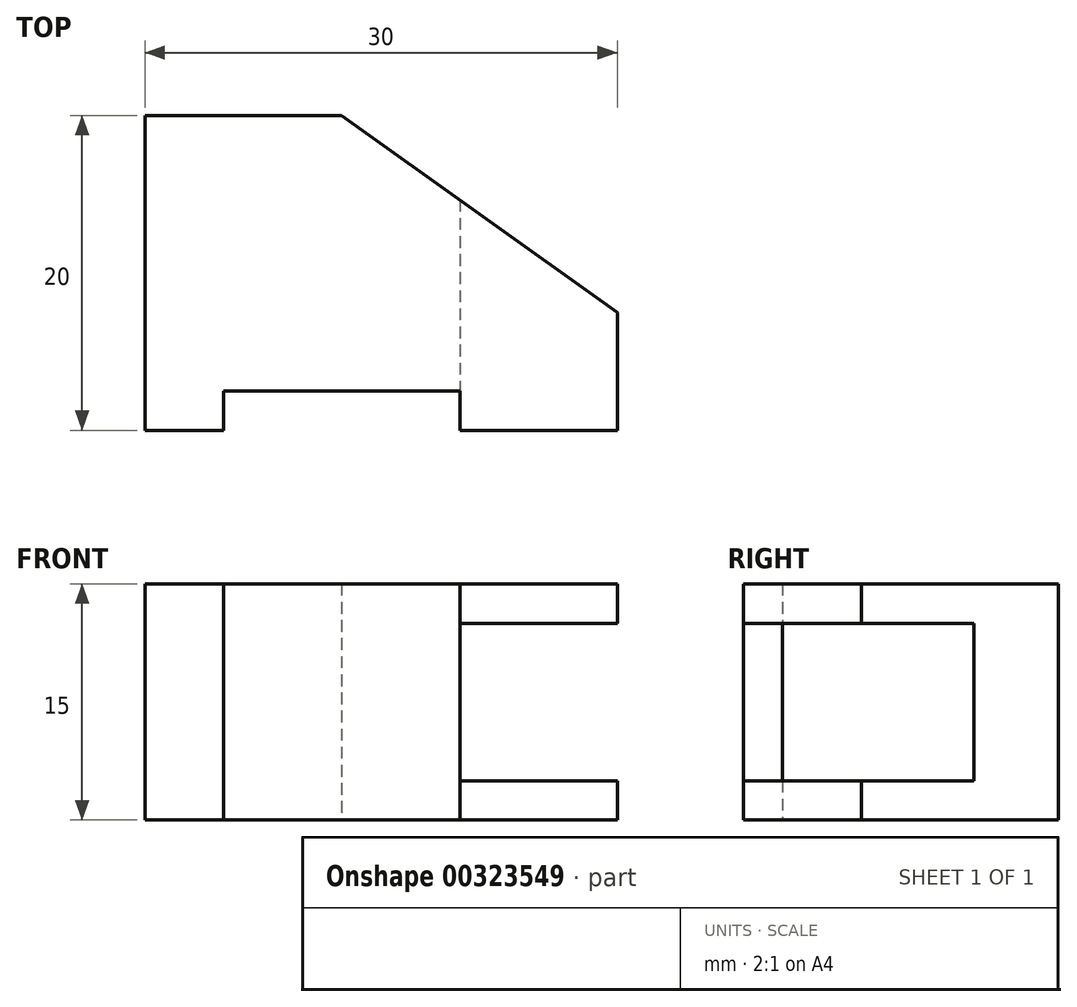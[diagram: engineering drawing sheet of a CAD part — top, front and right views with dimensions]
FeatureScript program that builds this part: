
annotation { "Feature Type Name" : "Feature", "Feature Type Description" : "" }
export const myFeature = defineFeature(function(context is Context, id is Id, definition is map)
    precondition{}
    {
        {
            var Q0;
            Q0=qCreatedBy(makeId("Top.planeOp"),FACE);
            var sketch = newSketch(context, id + "F0", { "sketchPlane" : qUnion([Q0])});
            skLineSegment(sketch, "E0", {"start": v(0, 0) * mm, "end": v(0, 20) * mm});
            skLineSegment(sketch, "E1", {"start": v(0, 20) * mm, "end": v(12.5, 20) * mm});
            skLineSegment(sketch, "E2", {"start": v(12.5, 20) * mm, "end": v(30, 7.5) * mm});
            skLineSegment(sketch, "E3", {"start": v(30, 7.5) * mm, "end": v(30, 0) * mm});
            skLineSegment(sketch, "E4", {"start": v(30, 0) * mm, "end": v(20, 0) * mm});
            skLineSegment(sketch, "E5", {"start": v(20, 0) * mm, "end": v(20, 2.5) * mm});
            skLineSegment(sketch, "E6", {"start": v(20, 2.5) * mm, "end": v(5, 2.5) * mm});
            skLineSegment(sketch, "E7", {"start": v(5, 2.5) * mm, "end": v(5, 0) * mm});
            skLineSegment(sketch, "E8", {"start": v(5, 0) * mm, "end": v(0, 0) * mm});
            skSolve(sketch);
        }
        {
            var Q0;
            Q0 = qSketchRegion(id + "F0", true);
            extrude(context, id + "F1", {"entities" : qUnion([Q0]), "depth" : 2.5 * mm});
        }
        {
            var Q0;
            Q0=makeQuery(id+"F1.opExtrude","CAP_FACE",FACE,{"disambiguationData":[OSD([sQuery(id+"F0.wireOp",EDGE,"E0"),sQuery(id+"F0.wireOp",EDGE,"E1"),sQuery(id+"F0.wireOp",EDGE,"E2"),sQuery(id+"F0.wireOp",EDGE,"E3"),sQuery(id+"F0.wireOp",EDGE,"E4"),sQuery(id+"F0.wireOp",EDGE,"E5"),sQuery(id+"F0.wireOp",EDGE,"E6"),sQuery(id+"F0.wireOp",EDGE,"E7"),sQuery(id+"F0.wireOp",EDGE,"E8")])],"isStart":false});
            var sketch = newSketch(context, id + "F2", { "sketchPlane" : qUnion([Q0])});
            skLineSegment(sketch, "E9", {"start": v(0, 0) * mm, "end": v(0, 20) * mm});
            skLineSegment(sketch, "E10", {"start": v(0, 20) * mm, "end": v(12.5, 20) * mm});
            skLineSegment(sketch, "E11", {"start": v(12.5, 20) * mm, "end": v(20, 14.64) * mm});
            skLineSegment(sketch, "E12", {"start": v(20, 14.64) * mm, "end": v(20, 0) * mm});
            skLineSegment(sketch, "E13", {"start": v(20, 0) * mm, "end": v(20, 2.5) * mm});
            skLineSegment(sketch, "E14", {"start": v(20, 2.5) * mm, "end": v(5, 2.5) * mm});
            skLineSegment(sketch, "E15", {"start": v(5, 2.5) * mm, "end": v(5, 0) * mm});
            skLineSegment(sketch, "E16", {"start": v(5, 0) * mm, "end": v(0, 0) * mm});
            skSolve(sketch);
        }
        {
            var Q0;
            Q0 = qSketchRegion(id + "F2", true);
            extrude(context, id + "F3", {"entities" : qUnion([Q0]), "operationType" : NewBodyOperationType.ADD, "depth" : 10 * mm});
        }
        {
            var Q0;
            Q0=makeQuery(id+"F3.opExtrude","CAP_FACE",FACE,{"disambiguationData":[OSD([sQuery(id+"F2.wireOp",EDGE,"E9"),sQuery(id+"F2.wireOp",EDGE,"E10"),sQuery(id+"F2.wireOp",EDGE,"E11"),sQuery(id+"F2.wireOp",EDGE,"E12"),sQuery(id+"F2.wireOp",EDGE,"E14"),sQuery(id+"F2.wireOp",EDGE,"E15"),sQuery(id+"F2.wireOp",EDGE,"E16")])],"isStart":false});
            var sketch = newSketch(context, id + "F4", { "sketchPlane" : qUnion([Q0])});
            skLineSegment(sketch, "E17", {"start": v(0, 0) * mm, "end": v(0, 20) * mm});
            skLineSegment(sketch, "E18", {"start": v(0, 20) * mm, "end": v(12.5, 20) * mm});
            skLineSegment(sketch, "E19", {"start": v(12.5, 20) * mm, "end": v(30, 7.5) * mm});
            skLineSegment(sketch, "E20", {"start": v(30, 7.5) * mm, "end": v(30, 0) * mm});
            skLineSegment(sketch, "E21", {"start": v(30, 0) * mm, "end": v(20, 0) * mm});
            skLineSegment(sketch, "E22", {"start": v(20, 0) * mm, "end": v(20, 2.5) * mm});
            skLineSegment(sketch, "E23", {"start": v(20, 2.5) * mm, "end": v(5, 2.5) * mm});
            skLineSegment(sketch, "E24", {"start": v(5, 2.5) * mm, "end": v(5, 0) * mm});
            skLineSegment(sketch, "E25", {"start": v(5, 0) * mm, "end": v(0, 0) * mm});
            skSolve(sketch);
        }
        {
            var Q0;
            Q0 = qSketchRegion(id + "F4", true);
            extrude(context, id + "F5", {"entities" : qUnion([Q0]), "operationType" : NewBodyOperationType.ADD, "depth" : 2.5 * mm});
        }
    });
